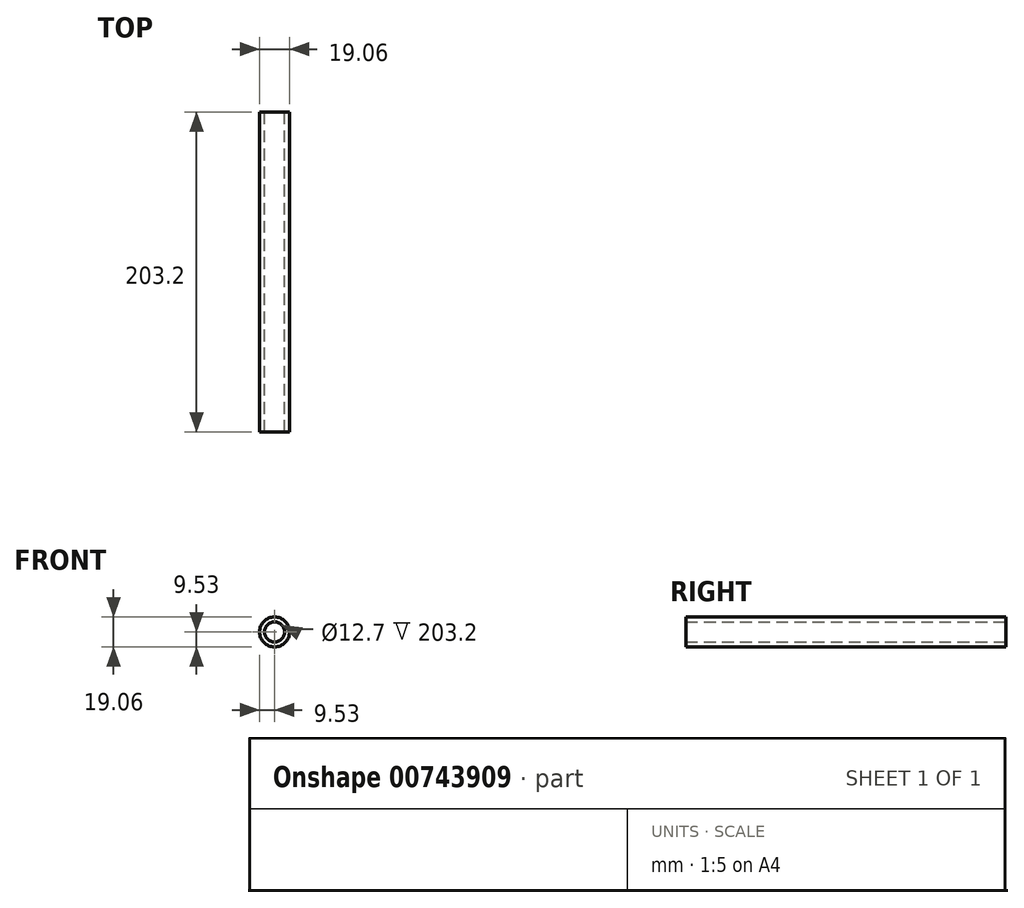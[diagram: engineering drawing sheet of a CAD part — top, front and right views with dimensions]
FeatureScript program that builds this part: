
annotation { "Feature Type Name" : "Feature", "Feature Type Description" : "" }
export const myFeature = defineFeature(function(context is Context, id is Id, definition is map)
    precondition{}
    {
        {
            var Q0;
            Q0=qCreatedBy(makeId("Front.planeOp"),FACE);
            var sketch = newSketch(context, id + "F0", { "sketchPlane" : qUnion([Q0])});
            skCircle(sketch, "E0", {"center": v(0, 0) * mm, "radius": 9.53 * mm});
            skCircle(sketch, "E1", {"center": v(0, 0) * mm, "radius": 6.35 * mm});
            skSolve(sketch);
        }
        {
            var Q0;
            Q0=makeQuery(id+"F0.imprint","IMPRINT",FACE,{"disambiguationData":[TD([[makeQuery(id+"F0.imprint","IMPRINT",EDGE,{"derivedFrom":sQuery(id+"F0.wireOp",EDGE,"E0")}),1.0]])]});
            extrude(context, id + "F1", {"entities" : qUnion([Q0]), "depth" : 203.2 * mm, "offsetDistance" : 25.4 * mm});
        }
    });
